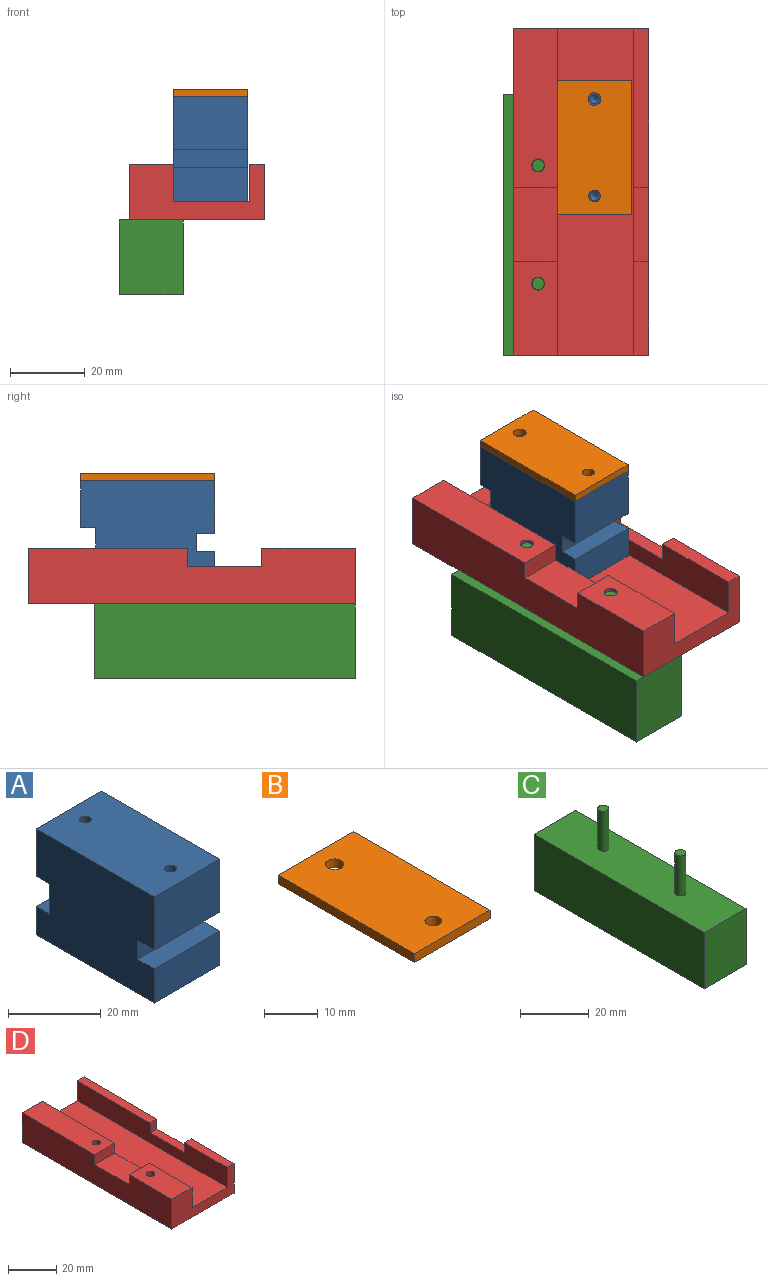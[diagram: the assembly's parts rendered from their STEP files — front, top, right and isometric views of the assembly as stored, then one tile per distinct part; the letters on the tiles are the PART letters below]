
ASSEMBLY  parts=4 mates=6
PART A: 18 faces, bbox 20x36x28 mm
  f0: plane 20x12.5mm, normal (0,1,0), area 250mm2, adj f1,f4,f5,f11
  f1: plane 36x28mm, normal (-1,0,0), area 951mm2, adj f0,f2,f3,f5,f6,f7,f8,f9
  f2: plane 20x14mm, normal (0,-1,0), area 280mm2, adj f1,f4,f5,f8
  f3: plane 36x20mm, normal (0,0,-1), area 720mm2, adj f1,f4,f6,f7
  f4: plane 36x28mm, normal (1,0,0), area 951mm2, adj f0,f2,f3,f5,f6,f7,f8,f9
  f5: plane 36x20mm, normal (0,0,1), area 710.2mm2, adj f0,f1,f2,f4,f15,f17
  f6: plane 20x9mm, normal (0,-1,0), area 180mm2, adj f1,f3,f4,f9
  f7: plane 20x7.5mm, normal (0,1,0), area 150mm2, adj f1,f3,f4,f12
  f8: plane 20x5mm, normal (0,0,-1), area 100mm2, adj f1,f2,f4,f10
  f9: plane 20x5mm, normal (0,0,1), area 100mm2, adj f1,f4,f6,f10
  f10: plane 20x5mm, normal (0,-1,0), area 100mm2, adj f1,f4,f8,f9
  f11: plane 20x4mm, normal (0,0,-1), area 80mm2, adj f0,f1,f4,f13
  f12: plane 20x4mm, normal (0,0,1), area 80mm2, adj f1,f4,f7,f13
  f13: plane 20x8mm, normal (0,1,0), area 160mm2, adj f1,f4,f11,f12
  f14: cone r=0mm half-angle=59deg, axis (0,0,1), area 5.7mm2, adj f15
  f15: cylinder r=1.25mm len=10mm, axis (0,0,1), area 78.5mm2, adj f5,f14
  f16: cone r=0mm half-angle=59deg, axis (0,0,1), area 5.7mm2, adj f17
  f17: cylinder r=1.25mm len=10mm, axis (0,0,1), area 78.5mm2, adj f5,f16
PART B: 8 faces, bbox 20x36x2 mm
  f0: plane 36x2mm, normal (-1,0,0), area 72mm2, adj f1,f3,f4,f5
  f1: plane 36x20mm, normal (0,0,-1), area 703.5mm2, adj f0,f2,f4,f5,f6,f7
  f2: plane 36x2mm, normal (1,0,0), area 72mm2, adj f1,f3,f4,f5
  f3: plane 36x20mm, normal (0,0,1), area 703.5mm2, adj f0,f2,f4,f5,f6,f7
  f4: plane 20x2mm, normal (0,-1,0), area 40mm2, adj f0,f1,f2,f3
  f5: plane 20x2mm, normal (0,1,0), area 40mm2, adj f0,f1,f2,f3
  f6: cylinder r=1.54mm len=3.08mm, axis (0,0,1), area 19.3mm2, adj f1,f3
  f7: cylinder r=1.7mm len=3.4mm, axis (0,0,1), area 21.4mm2, adj f1,f3
PART C: 10 faces, bbox 17.1x70x34.2 mm
  f0: plane 20x17.1mm, normal (0,1,0), area 342mm2, adj f1,f3,f4,f7
  f1: plane 70x20mm, normal (-1,0,0), area 1400mm2, adj f0,f2,f4,f7
  f2: plane 20x17.1mm, normal (0,-1,0), area 342mm2, adj f1,f3,f4,f7
  f3: plane 70x20mm, normal (1,0,0), area 1400mm2, adj f0,f2,f4,f7
  f4: plane 70x17.1mm, normal (0,0,-1), area 1197mm2, adj f0,f1,f2,f3
  f5: cylinder r=1.61mm len=14.2mm, axis (0,0,1), area 143.7mm2, adj f7,f8
  f6: cylinder r=1.6mm len=14.2mm, axis (0,0,1), area 142.8mm2, adj f7,f9
  f7: plane 70x17.1mm, normal (0,0,1), area 1180.8mm2, adj f0,f1,f2,f3,f5,f6
  f8: plane 3.22x3.22mm, normal (0,0,1), area 8.1mm2, adj f5
  f9: plane 3.2x3.2mm, normal (0,0,1), area 8mm2, adj f6
PART D: 20 faces, bbox 36.2x87.5x15 mm
  f0: plane 42.5x4mm, normal (0,0,1), area 170mm2, adj f3,f8,f10,f17
  f1: plane 42.5x11.7mm, normal (0,0,1), area 487.6mm2, adj f2,f4,f10,f11,f16
  f2: plane 87.5x15mm, normal (-1,0,0), area 1212.5mm2, adj f1,f6,f7,f9,f10,f14,f15,f16
  f3: plane 87.5x10mm, normal (-1,0,0), area 775mm2, adj f0,f5,f6,f10,f13,f17,f18,f19
  f4: plane 87.5x10mm, normal (1,0,0), area 775mm2, adj f1,f6,f9,f10,f13,f14,f15,f16
  f5: plane 25x4mm, normal (0,0,1), area 100mm2, adj f3,f6,f8,f18
  f6: plane 36.2x15mm, normal (0,-1,0), area 338mm2, adj f2,f3,f4,f5,f7,f8,f9,f13
  f7: plane 87.5x36.2mm, normal (0,0,-1), area 3148.3mm2, adj f2,f6,f8,f10,f11,f12
  f8: plane 87.5x15mm, normal (1,0,0), area 1212.5mm2, adj f0,f5,f6,f7,f10,f17,f18,f19
  f9: plane 25x11.7mm, normal (0,0,1), area 282.9mm2, adj f2,f4,f6,f12,f15
  f10: plane 36.2x15mm, normal (0,1,0), area 338mm2, adj f0,f1,f2,f3,f4,f7,f8,f13
  f11: cylinder r=1.75mm len=15mm, axis (0,0,-1), area 164.9mm2, adj f1,f7
  f12: cylinder r=1.75mm len=15mm, axis (0,0,-1), area 164.9mm2, adj f7,f9
  f13: plane 87.5x20.5mm, normal (0,0,1), area 1793.7mm2, adj f3,f4,f6,f10
  f14: plane 20x11.7mm, normal (0,0,1), area 234mm2, adj f2,f4,f15,f16
  f15: plane 11.7x5mm, normal (0,1,0), area 58.5mm2, adj f2,f4,f9,f14
  f16: plane 11.7x5mm, normal (0,-1,0), area 58.5mm2, adj f1,f2,f4,f14
  f17: plane 5x4mm, normal (0,-1,0), area 20mm2, adj f0,f3,f8,f19
  f18: plane 5x4mm, normal (0,1,0), area 20mm2, adj f3,f5,f8,f19
  f19: plane 20x4mm, normal (0,0,1), area 80mm2, adj f3,f8,f17,f18
PLACE A t=(11.06,88.4,-14.67)mm
PLACE B t=(11.06,88.4,13.33)mm
PLACE C t=(5.96,49.78,-39.67)mm
PLACE D t=(-0.64,102.28,-19.67)mm
MATE planar B.f1 <-> A.f5  axis (0,0,-1) through (21.06,70.37,13.33)mm
MATE planar A.f1 <-> D.f4  axis (-1,0,0) through (11.06,70.27,-0.52)mm
MATE planar D.f7 <-> C.f7  axis (0,0,-1) through (17.53,58.58,-19.67)mm
MATE cylindrical B.f6 <-> A.f14  axis (0,0,-1) through (21.06,57.4,13.33)mm
MATE planar A.f3 <-> D.f13  axis (0,0,-1) through (21.06,70.4,-14.67)mm
MATE cylindrical C.f5 <-> D.f12  axis (0,0,1) through (5.96,33.93,-12.57)mm
